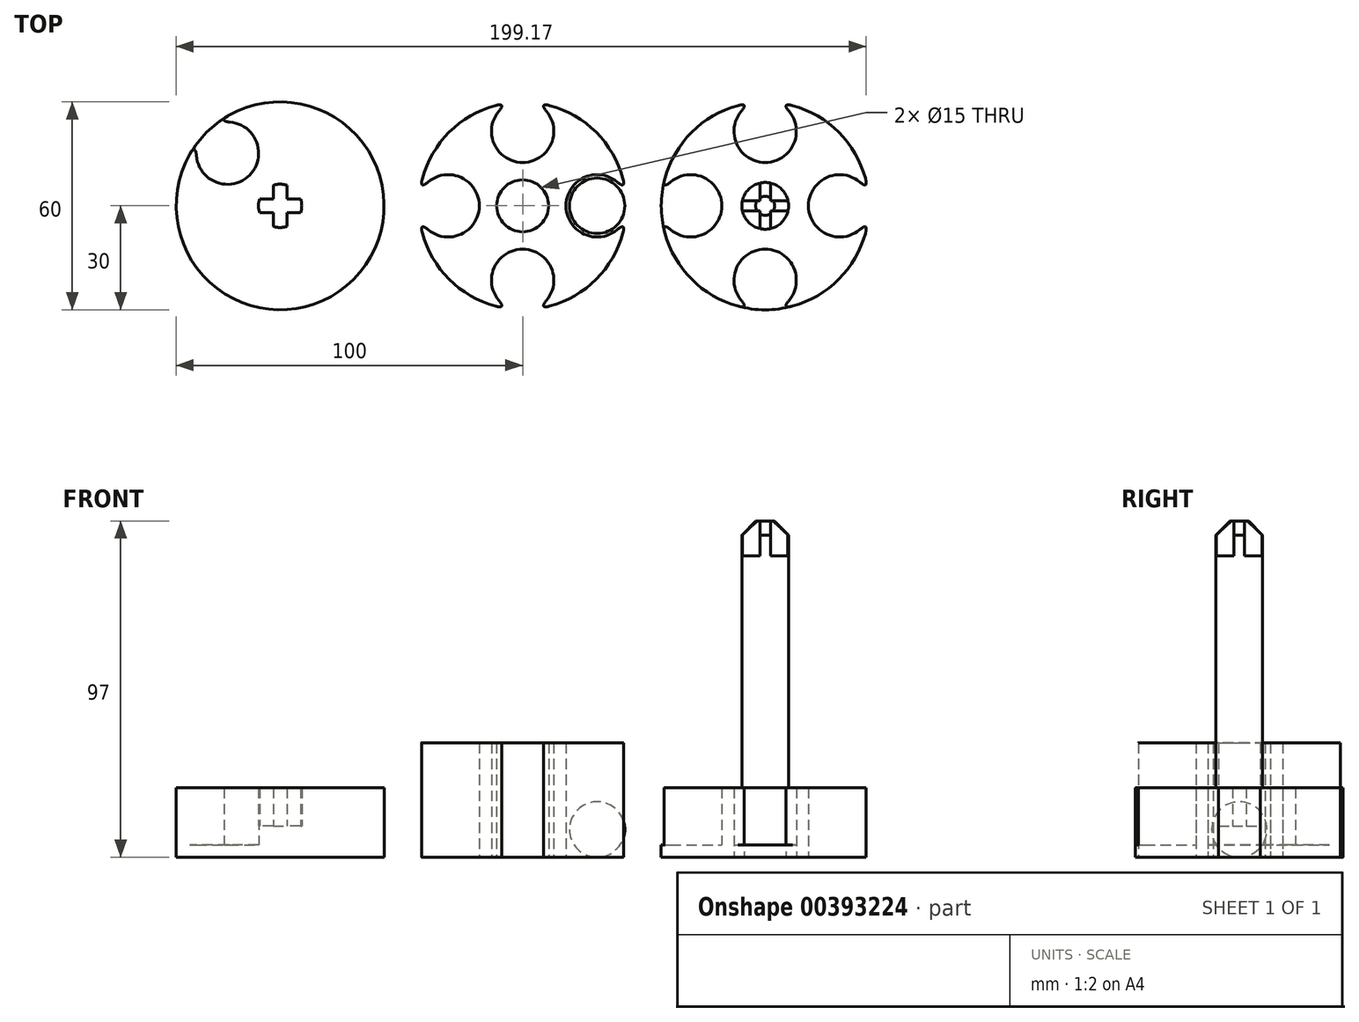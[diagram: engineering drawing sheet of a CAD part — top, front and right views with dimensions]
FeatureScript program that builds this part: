
annotation { "Feature Type Name" : "Feature", "Feature Type Description" : "" }
export const myFeature = defineFeature(function(context is Context, id is Id, definition is map)
    precondition{}
    {
        {
            var Q0;
            Q0=qCreatedBy(makeId("Top.planeOp"),FACE);
            var sketch = newSketch(context, id + "F0", { "sketchPlane" : qUnion([Q0])});
            skCircle(sketch, "E0", {"center": v(0, 0) * mm, "radius": 30 * mm});
            skArc(sketch, "E1", {"start": v(-29.8, -3.49) * mm, "mid": v(-12.5, 0) * mm, "end": v(-29.8, 3.49) * mm});
            skArc(sketch, "E2.MirrorC", {"start": v(29.8, -3.49) * mm, "mid": v(12.5, 0) * mm, "end": v(29.8, 3.49) * mm});
            skCircle(sketch, "E3", {"center": v(0, 0) * mm, "radius": 7.5 * mm});
            skArc(sketch, "E4", {"start": v(3.49, -29.8) * mm, "mid": v(0, -12.5) * mm, "end": v(-3.49, -29.8) * mm});
            skArc(sketch, "E5.MirrorC", {"start": v(3.49, 29.8) * mm, "mid": v(0, 12.5) * mm, "end": v(-3.49, 29.8) * mm});
            skArc(sketch, "E6.1.0.0", {"start": v(73.49, -29.8) * mm, "mid": v(70, -12.5) * mm, "end": v(66.51, -29.8) * mm});
            skArc(sketch, "E6.1.0.1", {"start": v(40.2, -3.49) * mm, "mid": v(57.5, 0) * mm, "end": v(40.2, 3.49) * mm});
            skArc(sketch, "E6.1.0.2", {"start": v(99.8, -3.49) * mm, "mid": v(82.5, 0) * mm, "end": v(99.8, 3.49) * mm});
            skArc(sketch, "E6.1.0.3", {"start": v(73.49, 29.8) * mm, "mid": v(70, 12.5) * mm, "end": v(66.51, 29.8) * mm});
            skCircle(sketch, "E6.1.0.4", {"center": v(70, 0) * mm, "radius": 30 * mm});
            skLineSegment(sketch, "E6.direction1", {"start": v(0, -21.5) * mm, "end": v(70, -21.5) * mm, "construction": true});
            skCircle(sketch, "E7", {"center": v(70, 0) * mm, "radius": 6.75 * mm});
            skLineSegment(sketch, "E8.left", {"start": v(71.5, -6.58) * mm, "end": v(71.5, -1.5) * mm});
            skLineSegment(sketch, "E8.right", {"start": v(68.5, -6.58) * mm, "end": v(68.5, -1.5) * mm});
            skLineSegment(sketch, "E9.bottom", {"start": v(76.58, -1.5) * mm, "end": v(71.5, -1.5) * mm});
            skLineSegment(sketch, "E9.top", {"start": v(76.58, 1.5) * mm, "end": v(71.5, 1.5) * mm});
            skLineSegment(sketch, "E10.trimOffspring", {"start": v(68.5, 1.5) * mm, "end": v(68.5, 6.58) * mm});
            skLineSegment(sketch, "E11.trimOffspring", {"start": v(68.5, 1.5) * mm, "end": v(63.42, 1.5) * mm});
            skLineSegment(sketch, "E12.trimOffspring", {"start": v(71.5, 1.5) * mm, "end": v(71.5, 6.58) * mm});
            skLineSegment(sketch, "E13.trimOffspring", {"start": v(68.5, -1.5) * mm, "end": v(63.42, -1.5) * mm});
            skCircle(sketch, "E14", {"center": v(-70, 0) * mm, "radius": 30 * mm});
            skLineSegment(sketch, "E15", {"start": v(-70, 0) * mm, "end": v(-100.4, 30.4) * mm, "construction": true});
            skArc(sketch, "E16", {"start": v(-93.54, 18.6) * mm, "mid": v(-78.84, 8.84) * mm, "end": v(-88.6, 23.54) * mm});
            skArc(sketch, "E17", {"start": v(-75.92, 2) * mm, "mid": v(-76.25, 0) * mm, "end": v(-75.92, -2) * mm});
            skLineSegment(sketch, "E18.left", {"start": v(-68, -5.92) * mm, "end": v(-68, -2) * mm});
            skLineSegment(sketch, "E18.right", {"start": v(-72, -5.92) * mm, "end": v(-72, -2) * mm});
            skLineSegment(sketch, "E19.bottom", {"start": v(-64.08, 2) * mm, "end": v(-68, 2) * mm});
            skLineSegment(sketch, "E19.top", {"start": v(-64.08, -2) * mm, "end": v(-68, -2) * mm});
            skLineSegment(sketch, "E20.trimOffspring", {"start": v(-72, 2) * mm, "end": v(-75.92, 2) * mm});
            skLineSegment(sketch, "E21.trimOffspring", {"start": v(-72, 2) * mm, "end": v(-72, 5.92) * mm});
            skLineSegment(sketch, "E22.trimOffspring", {"start": v(-72, -2) * mm, "end": v(-75.92, -2) * mm});
            skLineSegment(sketch, "E23.trimOffspring", {"start": v(-68, 2) * mm, "end": v(-68, 5.92) * mm});
            skArc(sketch, "E24.trimOffspring", {"start": v(-72, -5.92) * mm, "mid": v(-70, -6.25) * mm, "end": v(-68, -5.92) * mm});
            skArc(sketch, "E25.trimOffspring", {"start": v(-64.08, -2) * mm, "mid": v(-63.75, 0) * mm, "end": v(-64.08, 2) * mm});
            skArc(sketch, "E26.trimOffspring", {"start": v(-68, 5.92) * mm, "mid": v(-70, 6.25) * mm, "end": v(-72, 5.92) * mm});
            skSolve(sketch);
        }
        {
            var Q0;
            Q0=makeQuery(id+"F0.imprint","IMPRINT",FACE,{"disambiguationData":[TD([[makeQuery(id+"F0.imprint","IMPRINT",EDGE,{"derivedFrom":sQuery(id+"F0.wireOp",EDGE,"E3")}),-1.0]])]});
            var Q1;
            Q1=sQuery(id+"F0.wireOp",EDGE,"E0");
            extrude(context, id + "F1", {"entities" : qUnion([Q0]), "surfaceEntities" : qUnion([Q1]), "depth" : 33 * mm});
        }
        {
            var Q0;
            Q0=qCreatedBy(makeId("Top.planeOp"),FACE);
            var sketch = newSketch(context, id + "F2", { "sketchPlane" : qUnion([Q0])});
            skLineSegment(sketch, "E27", {"start": v(0, 0) * mm, "end": v(34, 0) * mm, "construction": true});
            skArc(sketch, "E28", {"start": v(9, 0) * mm, "mid": v(17, -8) * mm, "end": v(25, 0) * mm});
            skLineSegment(sketch, "E29", {"start": v(9, 0) * mm, "end": v(25, 0) * mm});
            skSolve(sketch);
        }
        {
            var Q0;
            Q0=makeQuery(id+"F2.imprint","IMPRINT",FACE,{"disambiguationData":[TD([[makeQuery(id+"F2.imprint","IMPRINT",EDGE,{"derivedFrom":sQuery(id+"F2.wireOp",EDGE,"E28")}),1.0]])]});
            var Q1;
            Q1=sQuery(id+"F2.wireOp",EDGE,"E27");
            revolve(context, id + "F3", {"entities" : qUnion([Q0]), "axis" : qUnion([Q1]), "revolveType" : RevolveType.FULL});
        }
        {
            var Q0;
            Q0=makeQuery(id+"F3.opRevolve","SWEPT_BODY",BODY,{"disambiguationData":[OSD([sQuery(id+"F2.wireOp",EDGE,"E28"),sQuery(id+"F2.wireOp",EDGE,"E29")])]});
            transform(context, id + "F4", {"entities" : qUnion([Q0]), "transformType" : TransformType.TRANSLATION_3D, "dx" : 4.5 * mm, "dy" : 0 * mm, "dz" : 8 * mm, "makeCopy" : false});
        }
        {
            var Q0;
            {var subQ1=sQuery(id+"F0.wireOp",EDGE,"E6.1.0.0");Q0=makeQuery(id+"F0.imprint","IMPRINT",FACE,{"disambiguationData":[TD([[makeQuery(id+"F0.imprint","IMPRINT",EDGE,{"derivedFrom":subQ1}),-1.0]])]});}
            var Q1;
            {var subQ0=sQuery(id+"F0.wireOp",EDGE,"E8.left");Q1=makeQuery(id+"F0.imprint","IMPRINT",FACE,{"disambiguationData":[TD([[makeQuery(id+"F0.imprint","IMPRINT",EDGE,{"derivedFrom":subQ0}),-1.0]])]});}
            var Q2;
            {var subQ4=sQuery(id+"F0.wireOp",EDGE,"E8.left");Q2=makeQuery(id+"F0.imprint","IMPRINT",FACE,{"disambiguationData":[TD([[makeQuery(id+"F0.imprint","IMPRINT",EDGE,{"derivedFrom":subQ4}),1.0]])]});}
            var Q3;
            {var subQ0=sQuery(id+"F0.wireOp",EDGE,"E8.right");Q3=makeQuery(id+"F0.imprint","IMPRINT",FACE,{"disambiguationData":[TD([[makeQuery(id+"F0.imprint","IMPRINT",EDGE,{"derivedFrom":subQ0}),1.0]])]});}
            var Q4;
            {var subQ0=sQuery(id+"F0.wireOp",EDGE,"E10.trimOffspring");Q4=makeQuery(id+"F0.imprint","IMPRINT",FACE,{"disambiguationData":[TD([[makeQuery(id+"F0.imprint","IMPRINT",EDGE,{"derivedFrom":subQ0}),1.0]])]});}
            var Q5;
            {var subQ0=sQuery(id+"F0.wireOp",EDGE,"E9.top");Q5=makeQuery(id+"F0.imprint","IMPRINT",FACE,{"disambiguationData":[TD([[makeQuery(id+"F0.imprint","IMPRINT",EDGE,{"derivedFrom":subQ0}),-1.0]])]});}
            extrude(context, id + "F5", {"entities" : qUnion([Q0, Q1, Q2, Q3, Q4, Q5]), "depth" : 20 * mm});
        }
        {
            var Q0;
            {var subQ0=sQuery(id+"F0.wireOp",EDGE,"E6.1.0.4");var subQ1=sQuery(id+"F0.wireOp",EDGE,"E6.1.0.1");var subQ2=makeQuery(id+"F0.imprint","INTERSECT",VERTEX,{"disambiguationData":[OD(0.0)],"derivedFrom":[subQ1,subQ0]});Q0=makeQuery(id+"F0.imprint","IMPRINT",FACE,{"disambiguationData":[TD([[makeQuery(id+"F0.imprint","IMPRINT",EDGE,{"disambiguationData":[TD([[subQ2,1.0]])],"derivedFrom":subQ1}),1.0]])]});}
            var Q1;
            {var subQ0=sQuery(id+"F0.wireOp",EDGE,"E6.1.0.4");var subQ1=sQuery(id+"F0.wireOp",EDGE,"E6.1.0.3");var subQ2=makeQuery(id+"F0.imprint","INTERSECT",VERTEX,{"disambiguationData":[OD(0.0)],"derivedFrom":[subQ1,subQ0]});Q1=makeQuery(id+"F0.imprint","IMPRINT",FACE,{"disambiguationData":[TD([[makeQuery(id+"F0.imprint","IMPRINT",EDGE,{"disambiguationData":[TD([[subQ2,-1.0]])],"derivedFrom":subQ1}),-1.0]])]});}
            var Q2;
            {var subQ0=sQuery(id+"F0.wireOp",EDGE,"E6.1.0.4");var subQ1=sQuery(id+"F0.wireOp",EDGE,"E6.1.0.2");var subQ2=makeQuery(id+"F0.imprint","INTERSECT",VERTEX,{"disambiguationData":[OD(0.0)],"derivedFrom":[subQ1,subQ0]});Q2=makeQuery(id+"F0.imprint","IMPRINT",FACE,{"disambiguationData":[TD([[makeQuery(id+"F0.imprint","IMPRINT",EDGE,{"disambiguationData":[TD([[subQ2,1.0]])],"derivedFrom":subQ1}),-1.0]])]});}
            var Q3;
            {var subQ0=sQuery(id+"F0.wireOp",EDGE,"E6.1.0.4");var subQ1=sQuery(id+"F0.wireOp",EDGE,"E6.1.0.0");var subQ2=makeQuery(id+"F0.imprint","INTERSECT",VERTEX,{"disambiguationData":[OD(0.0)],"derivedFrom":[subQ1,subQ0]});Q3=makeQuery(id+"F0.imprint","IMPRINT",FACE,{"disambiguationData":[TD([[makeQuery(id+"F0.imprint","IMPRINT",EDGE,{"disambiguationData":[TD([[subQ2,1.0]])],"derivedFrom":subQ1}),1.0]])]});}
            extrude(context, id + "F6", {"entities" : qUnion([Q0, Q1, Q2, Q3]), "operationType" : NewBodyOperationType.ADD, "depth" : 3.5 * mm});
        }
        {
            var Q0;
            Q0=makeQuery(id+"F0.imprint","IMPRINT",FACE,{"disambiguationData":[TD([[makeQuery(id+"F0.imprint","IMPRINT",EDGE,{"derivedFrom":sQuery(id+"F0.wireOp",EDGE,"E7")}),1.0]])]});
            var Q1;
            {var subQ0=sQuery(id+"F0.wireOp",EDGE,"E10.trimOffspring");Q1=makeQuery(id+"F0.imprint","IMPRINT",FACE,{"disambiguationData":[TD([[makeQuery(id+"F0.imprint","IMPRINT",EDGE,{"derivedFrom":subQ0}),1.0]])]});}
            var Q2;
            {var subQ0=sQuery(id+"F0.wireOp",EDGE,"E9.top");Q2=makeQuery(id+"F0.imprint","IMPRINT",FACE,{"disambiguationData":[TD([[makeQuery(id+"F0.imprint","IMPRINT",EDGE,{"derivedFrom":subQ0}),-1.0]])]});}
            var Q3;
            {var subQ0=sQuery(id+"F0.wireOp",EDGE,"E8.left");Q3=makeQuery(id+"F0.imprint","IMPRINT",FACE,{"disambiguationData":[TD([[makeQuery(id+"F0.imprint","IMPRINT",EDGE,{"derivedFrom":subQ0}),-1.0]])]});}
            var Q4;
            {var subQ0=sQuery(id+"F0.wireOp",EDGE,"E8.right");Q4=makeQuery(id+"F0.imprint","IMPRINT",FACE,{"disambiguationData":[TD([[makeQuery(id+"F0.imprint","IMPRINT",EDGE,{"derivedFrom":subQ0}),1.0]])]});}
            var Q5;
            Q5=sQuery(id+"F0.wireOp",EDGE,"E7");
            extrude(context, id + "F7", {"entities" : qUnion([Q0, Q1, Q2, Q3, Q4]), "operationType" : NewBodyOperationType.ADD, "surfaceEntities" : qUnion([Q5]), "depth" : 87 * mm});
        }
        {
            var Q0;
            {var subQ4=sQuery(id+"F0.wireOp",EDGE,"E8.left");Q0=makeQuery(id+"F0.imprint","IMPRINT",FACE,{"disambiguationData":[TD([[makeQuery(id+"F0.imprint","IMPRINT",EDGE,{"derivedFrom":subQ4}),1.0]])]});}
            extrude(context, id + "F8", {"entities" : qUnion([Q0]), "operationType" : NewBodyOperationType.ADD, "depth" : 97 * mm});
        }
        {
            var Q0;
            Q0=makeQuery(id+"F0.imprint","IMPRINT",FACE,{"disambiguationData":[TD([[makeQuery(id+"F0.imprint","IMPRINT",EDGE,{"derivedFrom":sQuery(id+"F0.wireOp",EDGE,"E17")}),-1.0]])]});
            var Q1;
            Q1=makeQuery(id+"F0.imprint","IMPRINT",FACE,{"disambiguationData":[TD([[makeQuery(id+"F0.imprint","IMPRINT",EDGE,{"derivedFrom":sQuery(id+"F0.wireOp",EDGE,"E17")}),1.0]])]});
            extrude(context, id + "F9", {"entities" : qUnion([Q0, Q1]), "depth" : 20 * mm});
        }
        {
            var Q0;
            {var subQ0=sQuery(id+"F0.wireOp",EDGE,"E16");var subQ1=sQuery(id+"F0.wireOp",EDGE,"E14");var subQ2=makeQuery(id+"F0.imprint","INTERSECT",VERTEX,{"disambiguationData":[OD(0.0)],"derivedFrom":[subQ1,subQ0]});Q0=makeQuery(id+"F0.imprint","IMPRINT",FACE,{"disambiguationData":[TD([[makeQuery(id+"F0.imprint","IMPRINT",EDGE,{"disambiguationData":[TD([[subQ2,1.0]])],"derivedFrom":subQ1}),1.0]])]});}
            extrude(context, id + "F10", {"entities" : qUnion([Q0]), "operationType" : NewBodyOperationType.ADD, "depth" : 3.5 * mm});
        }
        {
            var Q0;
            Q0=makeQuery(id+"F0.imprint","IMPRINT",FACE,{"disambiguationData":[TD([[makeQuery(id+"F0.imprint","IMPRINT",EDGE,{"derivedFrom":sQuery(id+"F0.wireOp",EDGE,"E17")}),1.0]])]});
            extrude(context, id + "F11", {"entities" : qUnion([Q0]), "operationType" : NewBodyOperationType.REMOVE, "depth" : 20 * mm, "hasSecondDirection" : true, "secondDirectionOppositeDirection" : false, "secondDirectionDepth" : 9 * mm});
        }
        {
            var Q0;
            {var subQ0=sQuery(id+"F0.wireOp",EDGE,"E2.MirrorC");var subQ1=sQuery(id+"F0.wireOp",EDGE,"E0");Q0=makeQuery(id+"F1.opExtrude","SWEPT_EDGE",EDGE,{"disambiguationData":[OSD([subQ1,subQ0]),TDD([makeQuery(id+"F0.imprint","INTERSECT",VERTEX,{"disambiguationData":[OD(1.0)],"derivedFrom":[subQ1,subQ0]})])]});}
            var Q1;
            {var subQ0=sQuery(id+"F0.wireOp",EDGE,"E2.MirrorC");var subQ1=sQuery(id+"F0.wireOp",EDGE,"E0");Q1=makeQuery(id+"F1.opExtrude","SWEPT_EDGE",EDGE,{"disambiguationData":[OSD([subQ1,subQ0]),TDD([makeQuery(id+"F0.imprint","INTERSECT",VERTEX,{"disambiguationData":[OD(0.0)],"derivedFrom":[subQ1,subQ0]})])]});}
            var Q2;
            {var subQ0=sQuery(id+"F0.wireOp",EDGE,"E5.MirrorC");var subQ1=sQuery(id+"F0.wireOp",EDGE,"E0");Q2=makeQuery(id+"F1.opExtrude","SWEPT_EDGE",EDGE,{"disambiguationData":[OSD([subQ1,subQ0]),TDD([makeQuery(id+"F0.imprint","INTERSECT",VERTEX,{"disambiguationData":[OD(0.0)],"derivedFrom":[subQ1,subQ0]})])]});}
            var Q3;
            {var subQ0=sQuery(id+"F0.wireOp",EDGE,"E5.MirrorC");var subQ1=sQuery(id+"F0.wireOp",EDGE,"E0");Q3=makeQuery(id+"F1.opExtrude","SWEPT_EDGE",EDGE,{"disambiguationData":[OSD([subQ1,subQ0]),TDD([makeQuery(id+"F0.imprint","INTERSECT",VERTEX,{"disambiguationData":[OD(1.0)],"derivedFrom":[subQ1,subQ0]})])]});}
            var Q4;
            {var subQ0=sQuery(id+"F0.wireOp",EDGE,"E1");var subQ1=sQuery(id+"F0.wireOp",EDGE,"E0");Q4=makeQuery(id+"F1.opExtrude","SWEPT_EDGE",EDGE,{"disambiguationData":[OSD([subQ1,subQ0]),TDD([makeQuery(id+"F0.imprint","INTERSECT",VERTEX,{"disambiguationData":[OD(0.0)],"derivedFrom":[subQ1,subQ0]})])]});}
            var Q5;
            {var subQ0=sQuery(id+"F0.wireOp",EDGE,"E1");var subQ1=sQuery(id+"F0.wireOp",EDGE,"E0");Q5=makeQuery(id+"F1.opExtrude","SWEPT_EDGE",EDGE,{"disambiguationData":[OSD([subQ1,subQ0]),TDD([makeQuery(id+"F0.imprint","INTERSECT",VERTEX,{"disambiguationData":[OD(1.0)],"derivedFrom":[subQ1,subQ0]})])]});}
            var Q6;
            {var subQ0=sQuery(id+"F0.wireOp",EDGE,"E4");var subQ1=sQuery(id+"F0.wireOp",EDGE,"E0");Q6=makeQuery(id+"F1.opExtrude","SWEPT_EDGE",EDGE,{"disambiguationData":[OSD([subQ1,subQ0]),TDD([makeQuery(id+"F0.imprint","INTERSECT",VERTEX,{"disambiguationData":[OD(0.0)],"derivedFrom":[subQ1,subQ0]})])]});}
            var Q7;
            {var subQ0=sQuery(id+"F0.wireOp",EDGE,"E4");var subQ1=sQuery(id+"F0.wireOp",EDGE,"E0");Q7=makeQuery(id+"F1.opExtrude","SWEPT_EDGE",EDGE,{"disambiguationData":[OSD([subQ1,subQ0]),TDD([makeQuery(id+"F0.imprint","INTERSECT",VERTEX,{"disambiguationData":[OD(1.0)],"derivedFrom":[subQ1,subQ0]})])]});}
            var Q8;
            {var subQ0=sQuery(id+"F0.wireOp",EDGE,"E6.1.0.4");var subQ1=sQuery(id+"F0.wireOp",EDGE,"E6.1.0.0");Q8=makeQuery(id+"F5.opExtrude","SWEPT_EDGE",EDGE,{"disambiguationData":[OSD([subQ1,subQ0]),TDD([makeQuery(id+"F0.imprint","INTERSECT",VERTEX,{"disambiguationData":[OD(0.0)],"derivedFrom":[subQ1,subQ0]})])]});}
            var Q9;
            {var subQ0=sQuery(id+"F0.wireOp",EDGE,"E6.1.0.4");var subQ1=sQuery(id+"F0.wireOp",EDGE,"E6.1.0.0");Q9=makeQuery(id+"F5.opExtrude","SWEPT_EDGE",EDGE,{"disambiguationData":[OSD([subQ1,subQ0]),TDD([makeQuery(id+"F0.imprint","INTERSECT",VERTEX,{"disambiguationData":[OD(1.0)],"derivedFrom":[subQ1,subQ0]})])]});}
            var Q10;
            {var subQ0=sQuery(id+"F0.wireOp",EDGE,"E6.1.0.4");var subQ1=sQuery(id+"F0.wireOp",EDGE,"E6.1.0.2");Q10=makeQuery(id+"F5.opExtrude","SWEPT_EDGE",EDGE,{"disambiguationData":[OSD([subQ1,subQ0]),TDD([makeQuery(id+"F0.imprint","INTERSECT",VERTEX,{"disambiguationData":[OD(1.0)],"derivedFrom":[subQ1,subQ0]})])]});}
            var Q11;
            {var subQ0=sQuery(id+"F0.wireOp",EDGE,"E6.1.0.4");var subQ1=sQuery(id+"F0.wireOp",EDGE,"E6.1.0.2");Q11=makeQuery(id+"F5.opExtrude","SWEPT_EDGE",EDGE,{"disambiguationData":[OSD([subQ1,subQ0]),TDD([makeQuery(id+"F0.imprint","INTERSECT",VERTEX,{"disambiguationData":[OD(0.0)],"derivedFrom":[subQ1,subQ0]})])]});}
            var Q12;
            {var subQ0=sQuery(id+"F0.wireOp",EDGE,"E6.1.0.4");var subQ1=sQuery(id+"F0.wireOp",EDGE,"E6.1.0.1");Q12=makeQuery(id+"F5.opExtrude","SWEPT_EDGE",EDGE,{"disambiguationData":[OSD([subQ1,subQ0]),TDD([makeQuery(id+"F0.imprint","INTERSECT",VERTEX,{"disambiguationData":[OD(0.0)],"derivedFrom":[subQ1,subQ0]})])]});}
            var Q13;
            {var subQ0=sQuery(id+"F0.wireOp",EDGE,"E6.1.0.4");var subQ1=sQuery(id+"F0.wireOp",EDGE,"E6.1.0.1");Q13=makeQuery(id+"F5.opExtrude","SWEPT_EDGE",EDGE,{"disambiguationData":[OSD([subQ1,subQ0]),TDD([makeQuery(id+"F0.imprint","INTERSECT",VERTEX,{"disambiguationData":[OD(1.0)],"derivedFrom":[subQ1,subQ0]})])]});}
            var Q14;
            {var subQ0=sQuery(id+"F0.wireOp",EDGE,"E6.1.0.4");var subQ1=sQuery(id+"F0.wireOp",EDGE,"E6.1.0.3");Q14=makeQuery(id+"F5.opExtrude","SWEPT_EDGE",EDGE,{"disambiguationData":[OSD([subQ1,subQ0]),TDD([makeQuery(id+"F0.imprint","INTERSECT",VERTEX,{"disambiguationData":[OD(1.0)],"derivedFrom":[subQ1,subQ0]})])]});}
            var Q15;
            {var subQ0=sQuery(id+"F0.wireOp",EDGE,"E6.1.0.4");var subQ1=sQuery(id+"F0.wireOp",EDGE,"E6.1.0.3");Q15=makeQuery(id+"F5.opExtrude","SWEPT_EDGE",EDGE,{"disambiguationData":[OSD([subQ1,subQ0]),TDD([makeQuery(id+"F0.imprint","INTERSECT",VERTEX,{"disambiguationData":[OD(0.0)],"derivedFrom":[subQ1,subQ0]})])]});}
            var Q16;
            {var subQ0=sQuery(id+"F0.wireOp",EDGE,"E16");var subQ1=sQuery(id+"F0.wireOp",EDGE,"E14");Q16=makeQuery(id+"F9.opExtrude","SWEPT_EDGE",EDGE,{"disambiguationData":[OSD([subQ1,subQ0]),TDD([makeQuery(id+"F0.imprint","INTERSECT",VERTEX,{"disambiguationData":[OD(1.0)],"derivedFrom":[subQ1,subQ0]})])]});}
            var Q17;
            {var subQ0=sQuery(id+"F0.wireOp",EDGE,"E16");var subQ1=sQuery(id+"F0.wireOp",EDGE,"E14");Q17=makeQuery(id+"F9.opExtrude","SWEPT_EDGE",EDGE,{"disambiguationData":[OSD([subQ1,subQ0]),TDD([makeQuery(id+"F0.imprint","INTERSECT",VERTEX,{"disambiguationData":[OD(0.0)],"derivedFrom":[subQ1,subQ0]})])]});}
            fillet(context, id + "F12", {"entities" : qUnion([Q0, Q1, Q2, Q3, Q4, Q5, Q6, Q7, Q8, Q9, Q10, Q11, Q12, Q13, Q14, Q15, Q16, Q17]), "radius" : 1 * mm, "tangentPropagation" : true, "rho" : 0.5, "crossSection" : FilletCrossSection.CONIC, "allowEdgeOverflow" : false});
        }
        {
            var Q0;
            {var subQ0=sQuery(id+"F0.wireOp",EDGE,"E7");Q0=makeQuery(id+"F8.opExtrude","CAP_EDGE",EDGE,{"disambiguationData":[OSD([subQ0]),TDD([makeQuery(id+"F0.imprint","IMPRINT",EDGE,{"disambiguationData":[TD([[makeQuery(id+"F0.imprint","INTERSECT",VERTEX,{"derivedFrom":[subQ0,sQuery(id+"F0.wireOp",EDGE,"E8.left")]}),1.0]])],"derivedFrom":subQ0})])],"isStart":false});}
            var Q1;
            {var subQ0=sQuery(id+"F0.wireOp",EDGE,"E7");Q1=makeQuery(id+"F8.opExtrude","CAP_EDGE",EDGE,{"disambiguationData":[OSD([subQ0]),TDD([makeQuery(id+"F0.imprint","IMPRINT",EDGE,{"disambiguationData":[TD([[makeQuery(id+"F0.imprint","INTERSECT",VERTEX,{"derivedFrom":[subQ0,sQuery(id+"F0.wireOp",EDGE,"E11.trimOffspring")]}),-1.0]])],"derivedFrom":subQ0})])],"isStart":false});}
            var Q2;
            {var subQ0=sQuery(id+"F0.wireOp",EDGE,"E7");Q2=makeQuery(id+"F8.opExtrude","CAP_EDGE",EDGE,{"disambiguationData":[OSD([subQ0]),TDD([makeQuery(id+"F0.imprint","IMPRINT",EDGE,{"disambiguationData":[TD([[makeQuery(id+"F0.imprint","INTERSECT",VERTEX,{"derivedFrom":[subQ0,sQuery(id+"F0.wireOp",EDGE,"E10.trimOffspring")]}),1.0]])],"derivedFrom":subQ0})])],"isStart":false});}
            var Q3;
            {var subQ0=sQuery(id+"F0.wireOp",EDGE,"E7");Q3=makeQuery(id+"F8.opExtrude","CAP_EDGE",EDGE,{"disambiguationData":[OSD([subQ0]),TDD([makeQuery(id+"F0.imprint","IMPRINT",EDGE,{"disambiguationData":[TD([[makeQuery(id+"F0.imprint","INTERSECT",VERTEX,{"derivedFrom":[subQ0,sQuery(id+"F0.wireOp",EDGE,"E9.bottom")]}),-1.0]])],"derivedFrom":subQ0})])],"isStart":false});}
            chamfer(context, id + "F13", {"entities" : qUnion([Q0, Q1, Q2, Q3]), "width" : 4 * mm, "tangentPropagation" : true});
        }
    });
